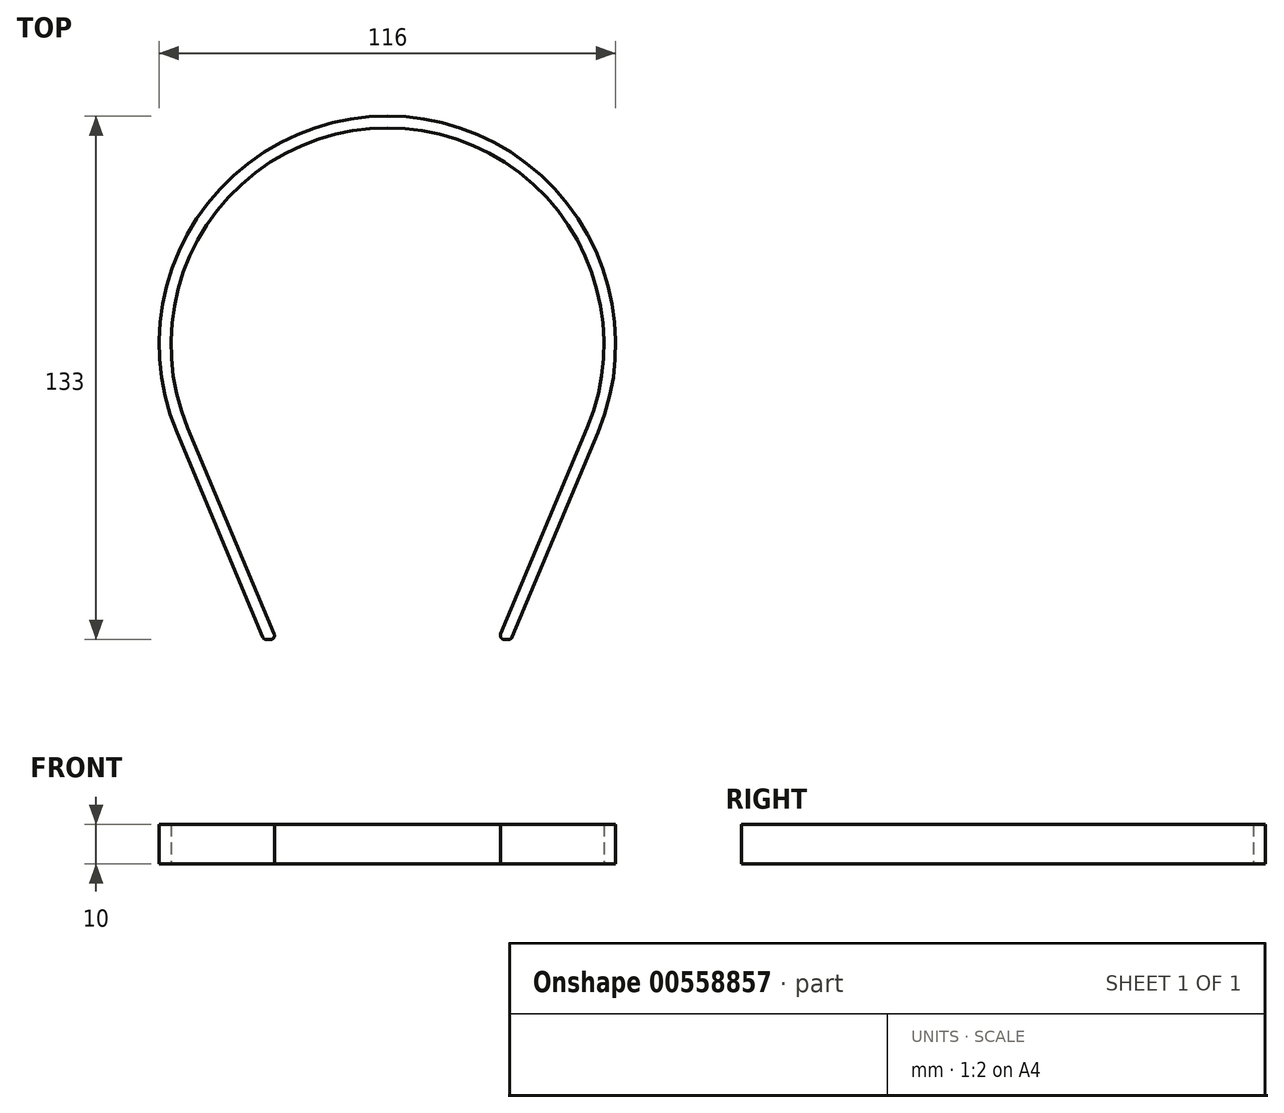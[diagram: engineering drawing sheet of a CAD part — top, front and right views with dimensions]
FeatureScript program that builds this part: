
annotation { "Feature Type Name" : "Feature", "Feature Type Description" : "" }
export const myFeature = defineFeature(function(context is Context, id is Id, definition is map)
    precondition{}
    {
        {
            var Q0;
            Q0=qCreatedBy(makeId("Top.planeOp"),FACE);
            var sketch = newSketch(context, id + "F0", { "sketchPlane" : qUnion([Q0])});
            skArc(sketch, "E0", {"start": v(42.7, 11.54) * mm, "mid": v(-8.02, 87.8) * mm, "end": v(-58.75, 11.54) * mm});
            skArc(sketch, "E1", {"start": v(45.46, 10.38) * mm, "mid": v(-8.02, 90.8) * mm, "end": v(-61.51, 10.38) * mm});
            skLineSegment(sketch, "E2", {"start": v(-8.02, 32.8) * mm, "end": v(-8.02, -117.2) * mm, "construction": true});
            skLineSegment(sketch, "E3", {"start": v(-39.73, -41.58) * mm, "end": v(-61.51, 10.38) * mm});
            skLineSegment(sketch, "E4", {"start": v(23.68, -41.58) * mm, "end": v(45.46, 10.38) * mm});
            skLineSegment(sketch, "E5", {"start": v(20.75, -40.8) * mm, "end": v(42.7, 11.54) * mm});
            skLineSegment(sketch, "E6.MirrorCS", {"start": v(-36.8, -40.8) * mm, "end": v(-58.75, 11.54) * mm});
            skPoint(sketch, "E7.trimOffspring.end.orphan", {"position": v(51.22, 31.88) * mm});
            skPoint(sketch, "E8.trimOffspring.end.orphan", {"position": v(-67.27, 31.88) * mm});
            skLineSegment(sketch, "E9", {"start": v(-38.8, -42.2) * mm, "end": v(-37.72, -42.2) * mm});
            skLineSegment(sketch, "E10.trimOffspring", {"start": v(21.67, -42.2) * mm, "end": v(22.76, -42.2) * mm});
            skPoint(sketch, "E11.orphan", {"position": v(9.73, -67.1) * mm});
            skPoint(sketch, "E12.orphan", {"position": v(-25.77, -67.1) * mm});
            skPoint(sketch, "E13.visualSharp", {"position": v(-39.47, -42.2) * mm});
            skArc(sketch, "E13.filletArc", {"start": v(-39.73, -41.58) * mm, "mid": v(-39.36, -42.03) * mm, "end": v(-38.8, -42.2) * mm});
            skPoint(sketch, "E14.visualSharp", {"position": v(-36.22, -42.2) * mm});
            skArc(sketch, "E14.filletArc", {"start": v(-37.72, -42.2) * mm, "mid": v(-36.89, -41.75) * mm, "end": v(-36.8, -40.8) * mm});
            skPoint(sketch, "E15.visualSharp", {"position": v(20.17, -42.2) * mm});
            skArc(sketch, "E15.filletArc", {"start": v(20.75, -40.8) * mm, "mid": v(20.84, -41.75) * mm, "end": v(21.67, -42.2) * mm});
            skPoint(sketch, "E16.visualSharp", {"position": v(23.42, -42.2) * mm});
            skArc(sketch, "E16.filletArc", {"start": v(22.76, -42.2) * mm, "mid": v(23.31, -42.03) * mm, "end": v(23.68, -41.58) * mm});
            skSolve(sketch);
        }
        {
            var Q0;
            Q0 = qSketchRegion(id + "F0", true);
            extrude(context, id + "F1", {"entities" : qUnion([Q0]), "depth" : 10 * mm, "offsetDistance" : 25 * mm});
        }
    });
